# Revit family: AFX-Jaxx-Wall_Sconce+++
name_source: partatom
category: Lighting Fixtures
units: mm (PartAtom-declared; Revit-internal decimal feet)

## family parameters
Cut with Voids When Loaded = No
Host = Face
Light Source = No
Part Type = Normal
Room Calculation Point = No
Round Connector Dimension = Use Diameter
Shared = No

## types (3) — shared parameters
Apparent Load = 0 VA
Assembly Code = D5020200
Bar Dist = 13/16"
Color Rendering Index = 90
Default Elevation = 48"
Depth = 9 1/4"
Lamp = LED
Length = 18"
Manufacturer = AFX Inc
Product Documentation Link = https://www.afxinc.com
Revit Model Built By = https://servex-us.com
Screen Finish = AFX - Diffuser
Type Comments = JAXX
URL = https://www.afxinc.com
Voltage = 120 V
Wattage Comments = 25W
Width = 5 1/8"

## per-type parameters (varying)
| type | Body Finish | Description | Type |
| JAXF2020L30D1SB | AFX - Satin Brass | 15'' LED Semi-Flush, Satin Brass | Jaxx_beam : JAXF2020L30D1SB |
| JAXF2020L30D1BK | AFX - Powdercoat Black | 15'' LED Semi-Flush, Black | Jaxx_beam : JAXF2020L30D1BK |
| JAXF2020L30D1PC | AFX - Polished Chrome | 15'' LED Semi-Flush, Polished Chrome | Jaxx_beam : JAXF2020L30D1PC |

note: column(s) folded — value = type name in every type: Model

## geometry (parser evidence)
native form markers: Sweep x5
no freeform markers — native parametric forms only
